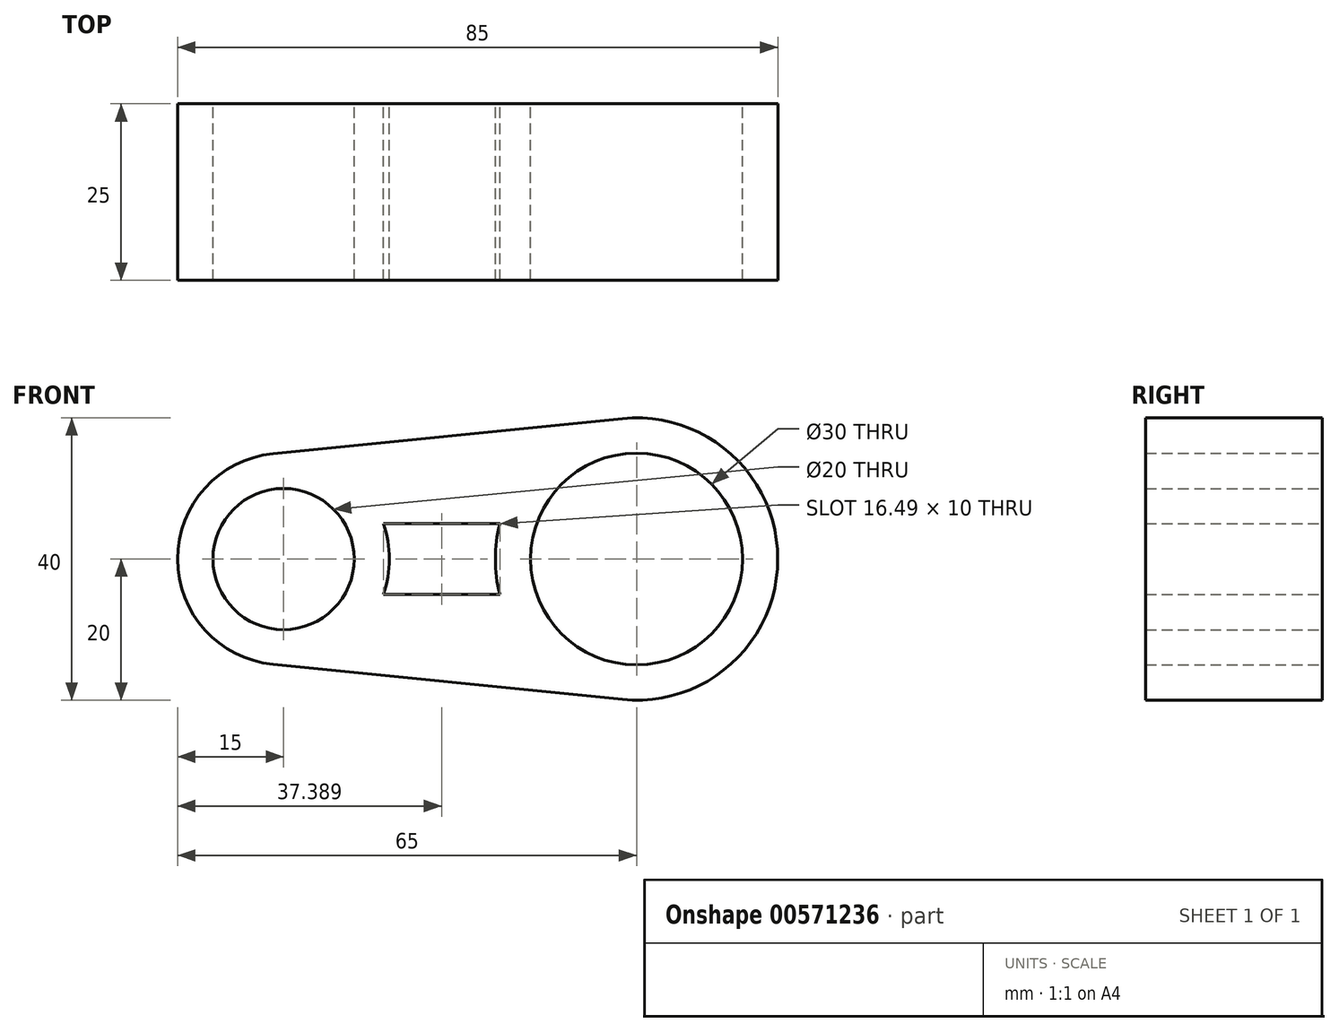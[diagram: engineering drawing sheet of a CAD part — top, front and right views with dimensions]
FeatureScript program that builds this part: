
annotation { "Feature Type Name" : "Feature", "Feature Type Description" : "" }
export const myFeature = defineFeature(function(context is Context, id is Id, definition is map)
    precondition{}
    {
        {
            var Q0;
            Q0=qCreatedBy(makeId("Front.planeOp"),FACE);
            var sketch = newSketch(context, id + "F0", { "sketchPlane" : qUnion([Q0])});
            skCircle(sketch, "E0", {"center": v(0, 0) * mm, "radius": 10 * mm});
            skCircle(sketch, "E1", {"center": v(0, 0) * mm, "radius": 15 * mm});
            skLineSegment(sketch, "E2", {"start": v(0, 0) * mm, "end": v(50, 0) * mm, "construction": true});
            skCircle(sketch, "E3", {"center": v(50, 0) * mm, "radius": 15 * mm});
            skCircle(sketch, "E4", {"center": v(50, 0) * mm, "radius": 20 * mm});
            skLineSegment(sketch, "E5", {"start": v(14.14, -5) * mm, "end": v(30.64, -5) * mm});
            skLineSegment(sketch, "E6", {"start": v(14.14, 5) * mm, "end": v(30.64, 5) * mm});
            skLineSegment(sketch, "E7", {"start": v(-1.5, -14.92) * mm, "end": v(48, -19.9) * mm});
            skLineSegment(sketch, "E8", {"start": v(-1.5, 14.92) * mm, "end": v(48, 19.9) * mm});
            skSolve(sketch);
        }
        {
            var Q0;
            Q0 = qSketchRegion(id + "F0", true);
            extrude(context, id + "F1", {"entities" : qUnion([Q0]), "depth" : 25 * mm, "offsetDistance" : 25 * mm});
        }
    });
